# Revit family: Curb_Solid_NobleCompany
name_source: partatom
category: Specialty Equipment
revit_build: Autodesk Revit 2014 (Build: 20140709_2115(x64)
units: mm (PartAtom-declared; Revit-internal decimal feet)

## types (3) — shared parameters
Assembly Code = D2030300
Base = Polymer coated Expanded Polystyrene
Building Codes = http://www.noblecompany.com
Default Elevation = 0"
Height = 20"
Installation-Fabrication = http://www.noblecompany.com
Manufacturer = Noble Company
Manufacturer Fax = 231-799-8850
Product Data = http://www.noblecompany.com
Product Properties = http://www.noblecompany.com
Radius = 15 1/2"
URL = www.noblecompany.com

## per-type parameters (varying)
| type | 1 Side | 2 Sides | 3 Sides | Description | Det2 | Model | Type Comments |
| 1 Sided | Yes | No | No | Noble Preformed Curb | No | Preformed Curb |  |
| 2 Sided | No | Yes | No | Noble Preformed Overlay Curb | Yes | Preformed Overlay Curb |  |
| 3 Sided | No | No | Yes | Noble Preformed Overlay Curb | Yes | Preformed Overlay Curb | Modify Sweep for Neo Angles and Custom Applications |

## geometry (parser evidence)
native form markers: Sweep x3
no freeform markers — native parametric forms only
